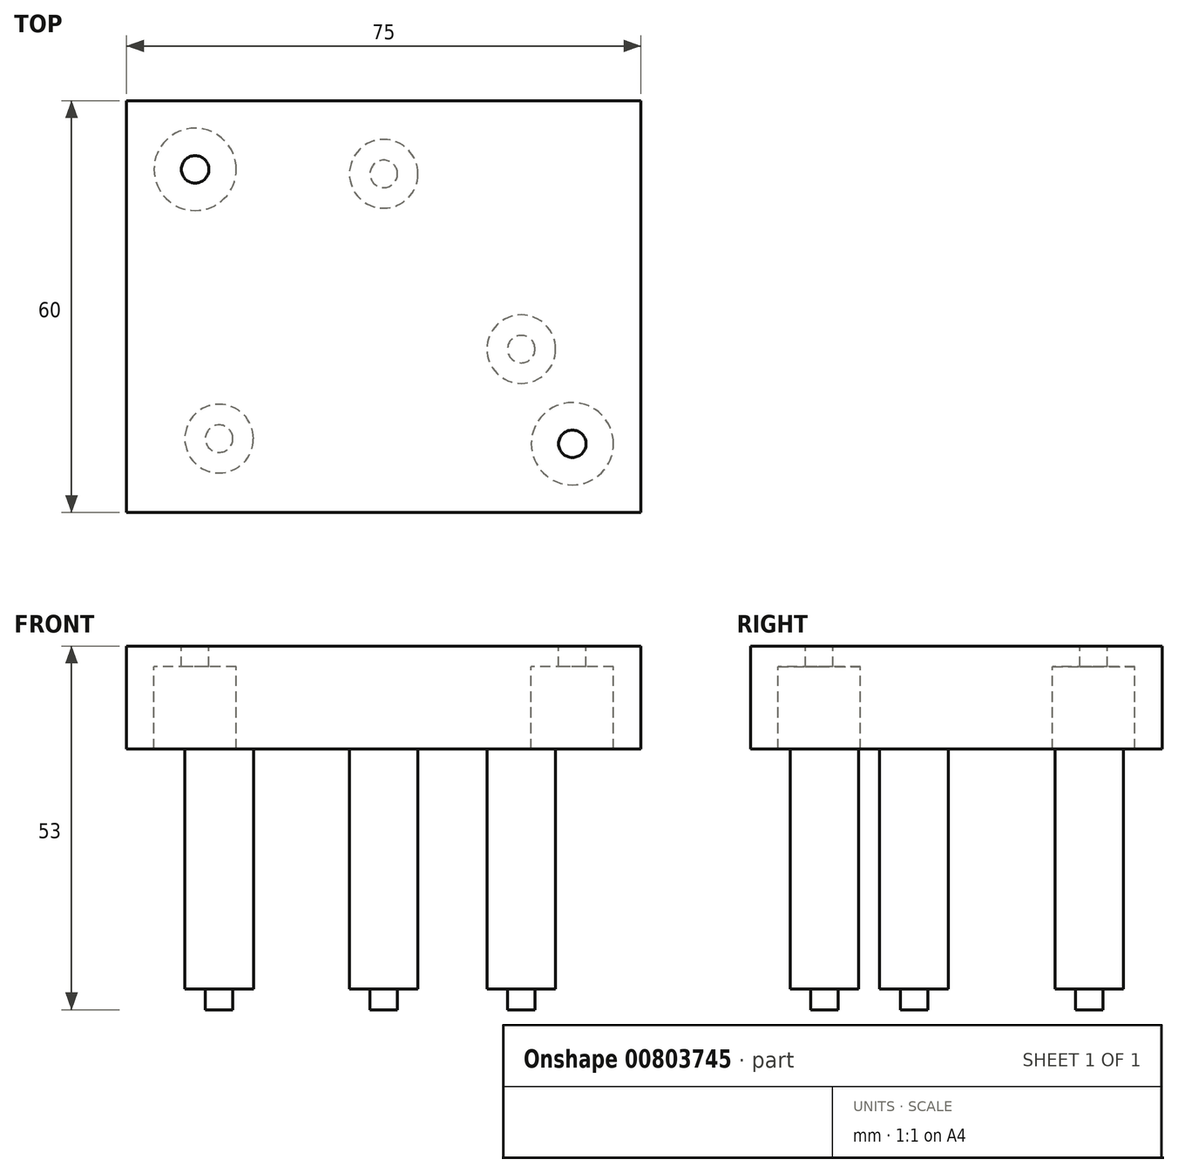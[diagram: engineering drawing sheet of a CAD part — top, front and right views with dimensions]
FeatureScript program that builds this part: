
annotation { "Feature Type Name" : "Feature", "Feature Type Description" : "" }
export const myFeature = defineFeature(function(context is Context, id is Id, definition is map)
    precondition{}
    {
        {
            var Q0;
            Q0=qCreatedBy(makeId("Top.planeOp"),FACE);
            var sketch = newSketch(context, id + "F0", { "sketchPlane" : qUnion([Q0])});
            skLineSegment(sketch, "E0.bottom", {"start": v(37.5, 30) * mm, "end": v(-37.5, 30) * mm});
            skLineSegment(sketch, "E0.top", {"start": v(37.5, -30) * mm, "end": v(-37.5, -30) * mm});
            skLineSegment(sketch, "E0.left", {"start": v(37.5, 30) * mm, "end": v(37.5, -30) * mm});
            skLineSegment(sketch, "E0.right", {"start": v(-37.5, 30) * mm, "end": v(-37.5, -30) * mm});
            skPoint(sketch, "E0.middle", {"position": v(0, 0) * mm});
            skLineSegment(sketch, "E1", {"start": v(0, 0) * mm, "end": v(0, 19.35) * mm});
            skLineSegment(sketch, "E2", {"start": v(0, 0) * mm, "end": v(20.05, 0) * mm});
            skLineSegment(sketch, "E3", {"start": v(20.05, 0) * mm, "end": v(20.05, -6.2) * mm});
            skLineSegment(sketch, "E4", {"start": v(0, 0) * mm, "end": v(-24, 0) * mm});
            skLineSegment(sketch, "E5", {"start": v(-24, 0) * mm, "end": v(-24, -19.25) * mm});
            skCircle(sketch, "E6", {"center": v(0, 19.35) * mm, "radius": 5 * mm});
            skCircle(sketch, "E7", {"center": v(0, 19.35) * mm, "radius": 2 * mm});
            skCircle(sketch, "E8", {"center": v(20.05, -6.2) * mm, "radius": 5 * mm});
            skCircle(sketch, "E9", {"center": v(20.05, -6.2) * mm, "radius": 2 * mm});
            skCircle(sketch, "E10", {"center": v(-24, -19.25) * mm, "radius": 5 * mm});
            skCircle(sketch, "E11", {"center": v(-24, -19.25) * mm, "radius": 2 * mm});
            skLineSegment(sketch, "E12.bottom", {"start": v(-37.5, 30) * mm, "end": v(-27.5, 30) * mm});
            skLineSegment(sketch, "E12.top", {"start": v(-37.5, 20) * mm, "end": v(-27.5, 20) * mm});
            skLineSegment(sketch, "E12.left", {"start": v(-37.5, 30) * mm, "end": v(-37.5, 20) * mm});
            skLineSegment(sketch, "E12.right", {"start": v(-27.5, 30) * mm, "end": v(-27.5, 20) * mm});
            skLineSegment(sketch, "E13.bottom", {"start": v(37.5, -30) * mm, "end": v(27.5, -30) * mm});
            skLineSegment(sketch, "E13.top", {"start": v(37.5, -20) * mm, "end": v(27.5, -20) * mm});
            skLineSegment(sketch, "E13.left", {"start": v(37.5, -30) * mm, "end": v(37.5, -20) * mm});
            skLineSegment(sketch, "E13.right", {"start": v(27.5, -30) * mm, "end": v(27.5, -20) * mm});
            skCircle(sketch, "E14", {"center": v(-27.5, 20) * mm, "radius": 6 * mm});
            skCircle(sketch, "E15", {"center": v(-27.5, 20) * mm, "radius": 2 * mm});
            skCircle(sketch, "E16", {"center": v(27.5, -20) * mm, "radius": 6 * mm});
            skCircle(sketch, "E17", {"center": v(27.5, -20) * mm, "radius": 2 * mm});
            skSolve(sketch);
        }
        {
            var Q0;
            Q0=qSketchRegion(id+"F0",true);
            extrude(context, id + "F1", {"entities" : qUnion([Q0]), "depth" : -15 * mm, "offsetDistance" : 25 * mm});
        }
        {
            var Q0;
            {var subQ0=sQuery(id+"F0.wireOp",EDGE,"E14");var subQ1=sQuery(id+"F0.wireOp",EDGE,"E12.top");var subQ2=makeQuery(id+"F0.imprint","INTERSECT",VERTEX,{"derivedFrom":[subQ1,subQ0]});Q0=makeQuery(id+"F0.imprint","IMPRINT",FACE,{"disambiguationData":[TD([[makeQuery(id+"F0.imprint","IMPRINT",EDGE,{"disambiguationData":[TD([[subQ2,-1.0]])],"derivedFrom":subQ1}),-1.0]])]});}
            var Q1;
            {var subQ0=sQuery(id+"F0.wireOp",EDGE,"E14");var subQ1=sQuery(id+"F0.wireOp",EDGE,"E12.top");var subQ2=makeQuery(id+"F0.imprint","INTERSECT",VERTEX,{"derivedFrom":[subQ1,subQ0]});Q1=makeQuery(id+"F0.imprint","IMPRINT",FACE,{"disambiguationData":[TD([[makeQuery(id+"F0.imprint","IMPRINT",EDGE,{"disambiguationData":[TD([[subQ2,-1.0]])],"derivedFrom":subQ1}),1.0]])]});}
            var Q2;
            {var subQ0=sQuery(id+"F0.wireOp",EDGE,"E16");var subQ1=sQuery(id+"F0.wireOp",EDGE,"E13.top");var subQ2=makeQuery(id+"F0.imprint","INTERSECT",VERTEX,{"derivedFrom":[subQ1,subQ0]});Q2=makeQuery(id+"F0.imprint","IMPRINT",FACE,{"disambiguationData":[TD([[makeQuery(id+"F0.imprint","IMPRINT",EDGE,{"disambiguationData":[TD([[subQ2,-1.0]])],"derivedFrom":subQ1}),1.0]])]});}
            var Q3;
            {var subQ0=sQuery(id+"F0.wireOp",EDGE,"E16");var subQ1=sQuery(id+"F0.wireOp",EDGE,"E13.top");var subQ2=makeQuery(id+"F0.imprint","INTERSECT",VERTEX,{"derivedFrom":[subQ1,subQ0]});Q3=makeQuery(id+"F0.imprint","IMPRINT",FACE,{"disambiguationData":[TD([[makeQuery(id+"F0.imprint","IMPRINT",EDGE,{"disambiguationData":[TD([[subQ2,-1.0]])],"derivedFrom":subQ1}),-1.0]])]});}
            extrude(context, id + "F2", {"entities" : qUnion([Q0, Q1, Q2, Q3]), "operationType" : NewBodyOperationType.ADD, "depth" : -3 * mm, "offsetDistance" : 25 * mm});
        }
        {
            var Q0;
            Q0=makeQuery(id+"F0.imprint","IMPRINT",FACE,{"disambiguationData":[TD([[makeQuery(id+"F0.imprint","IMPRINT",EDGE,{"derivedFrom":sQuery(id+"F0.wireOp",EDGE,"E6")}),1.0]])]});
            var Q1;
            Q1=makeQuery(id+"F0.imprint","IMPRINT",FACE,{"disambiguationData":[TD([[makeQuery(id+"F0.imprint","IMPRINT",EDGE,{"derivedFrom":sQuery(id+"F0.wireOp",EDGE,"E10")}),1.0]])]});
            var Q2;
            Q2=makeQuery(id+"F0.imprint","IMPRINT",FACE,{"disambiguationData":[TD([[makeQuery(id+"F0.imprint","IMPRINT",EDGE,{"derivedFrom":sQuery(id+"F0.wireOp",EDGE,"E8")}),1.0]])]});
            extrude(context, id + "F3", {"entities" : qUnion([Q0, Q1, Q2]), "operationType" : NewBodyOperationType.ADD, "depth" : -50 * mm, "offsetDistance" : 25 * mm});
        }
        {
            var Q0;
            Q0=makeQuery(id+"F0.imprint","IMPRINT",FACE,{"disambiguationData":[TD([[makeQuery(id+"F0.imprint","IMPRINT",EDGE,{"derivedFrom":sQuery(id+"F0.wireOp",EDGE,"E7")}),1.0]])]});
            var Q1;
            Q1=makeQuery(id+"F0.imprint","IMPRINT",FACE,{"disambiguationData":[TD([[makeQuery(id+"F0.imprint","IMPRINT",EDGE,{"derivedFrom":sQuery(id+"F0.wireOp",EDGE,"E11")}),1.0]])]});
            var Q2;
            Q2=makeQuery(id+"F0.imprint","IMPRINT",FACE,{"disambiguationData":[TD([[makeQuery(id+"F0.imprint","IMPRINT",EDGE,{"derivedFrom":sQuery(id+"F0.wireOp",EDGE,"E9")}),1.0]])]});
            extrude(context, id + "F4", {"entities" : qUnion([Q0, Q1, Q2]), "operationType" : NewBodyOperationType.ADD, "depth" : -53 * mm, "offsetDistance" : 25 * mm});
        }
    });
